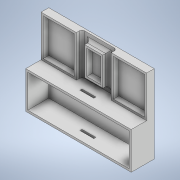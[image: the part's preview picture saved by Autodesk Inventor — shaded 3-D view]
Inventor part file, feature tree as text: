
AUTODESK INVENTOR PART (.ipt)
format: ipt  version: 2021 (Build 250183000, 183)  size: 189,952 bytes
history: native  units: mm
features: extrude x4, sketch x4, fillet x1
ambient origin geometry x8: Origin, YZ Plane, XZ Plane, XY Plane, X Axis, Y Axis, Z Axis, Center Point
bodies: Solid1 (feature_tree)
feature tree (9):
  extrude  "Extrusion1"  Depth=112.0mm
  extrude  "Extrusion2"  Depth=151.0mm
  extrude  "Extrusion3"  Depth=3.0mm
  fillet  "Fillet1"  Radius=3.0mm
  extrude  "Extrusion4"  Depth=3.0mm
  sketch  "Sketch1"  dims[d0=151.0mm d1=112.0mm]
  sketch  "Sketch2"  dims[d2=3.0mm d3=0.0mm d4=151.0mm]
  sketch  "Sketch3"  dims[d5=53.0mm d6=3.0mm d7=3.0mm]
  sketch  "Sketch5"  dims[d8=3.0mm d9=3.0mm d10=30.0mm d11=0.0mm d12=44.5mm d13=53.0mm d14=44.5mm d15=53.0mm d16=3.0mm d17=3.0mm d18=3.0mm d19=20.0mm d20=35.0mm d21=12.0mm d22=18.0mm d23=3.0mm d24=3.0mm d25=3.0mm d26=8.0mm d27=0.0mm d28=4.0mm d29=20.0mm d30=3.0mm d31=65.5mm d32=12.0mm d33=8.0mm d34=0.0mm]
